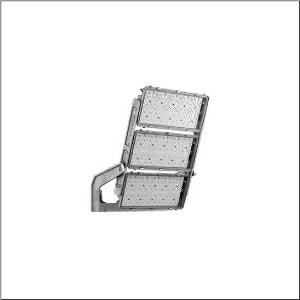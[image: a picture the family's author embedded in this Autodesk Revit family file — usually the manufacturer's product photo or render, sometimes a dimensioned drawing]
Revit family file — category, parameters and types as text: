
# Revit family: floodlight_fl_11_maxi_pro_remote___pl64_5xa779426v01aa_0b09
name_source: partatom
category: Lighting Fixtures
units: mm (PartAtom-declared; Revit-internal decimal feet)

## family parameters
Cut with Voids When Loaded = No
Host = Face
Light Source = No
Part Type = Normal
Room Calculation Point = No
Round Connector Dimension = Use Diameter
Shared = No

## types (1)
- --- (1 x LED, 216630 lm, 1539.7 W, 4000K)
    Apparent Load = 1540 VA
    CIE Flux Codes = 28 79 98 100 100
    Color Rendering = 70
    Color Temperature = 4000K
    Default Elevation = 1800 mm
    Description = Floodlight FL 11  maxi  pro Remote floodlight; light control with lens of PMMA; cover panel of toughened safety glass, transparent; light distribution: PL64, asymmetric direct distribution, LEDcolour temperature: 4000K, rated luminous flux: 216.630lm, colour rendering: CRI > 70, light colour: 740; luminous efficacy: 141lm/W; brightness control: DALI 2 (1 DALI address); with terminal, 8-pole, max. 2.5mm², mains connection: 220..240V/380..400V AC, 50/60Hz, surge voltage resistance: line to ground: 10kV, ECG replaceable separately, no afterglow with DALI off / DMX off command, LED unit replaceable without ESD environment, dustproof LED module, dimming range 10..100%; 1540W floodlight with 2x LED unit of diecast aluminium, coated grey; length: 713mm / width: 651mm / height: 338mm; mounting bracket, of diecast aluminium, uncoated, natural, equipment: Power, protection rating (complete): IP66; insulation class (complete): insulation class I (protective earthing); certification: CE, ENEC, VDE; ball protection: ball impact resistance with accessories, impact resistance: IK07; only for outdoor installations, rated ambient temperature 10°C, permissible operating ambient temperature: -40..+30°C, permissible storage temperature: -40..+85°Cpackaging unit: 1 piece

Light Distribution: PL64
    Height = 320 mm
    Lamp = 1 x LED
    Lamp Light Flux = 216630 lm
    Lamp Power = 1539.7 W
    Lamp count = 1
    Length = 1002 mm
    Luminous efficacy = 141 lm/W
    Manufacturer = Siteco
    ModVariant = No
    Model = 5XA779426V01AA
    Mounting Place = Ceiling
    Mounting Type = Surface mounted
    Number of Poles = 1
    OnlyDefault = Yes
    Power Factor = 1
    Product Name = Floodlight FL 11 maxi pro Remote | PL64
    Product group = floodlight | ceiling mounted
    ProductGroupID = 301
    Protection Class = Protection class I
    Protection Degree = IP 66
    RLX_Detail_Level = 1
    RLX_Emergency_Light_Flux = 0 lm
    RLX_Emergency_Type = 0
    RLX_Emergency_Type_DB = No
    RlxData = <blob elided: 52221 chars, md5=aefd5df7>
    Socket = socket
    Standby Power = 0 W
    System Light Flux = 216630 lm
    System Power = 1540 W
    Type Comments = factory setting: luminous flux: 100 % | dim-lin: 254 | 1080 mA
    Type Image = l_1349141.jpg
    URL = http://relux.com
    VarID = @adj_103068
    Voltage = 0 V
    Weight = 0.00 kg
    Width = 655 mm

## geometry (parser evidence)
native form markers: Blend x4, Sweep x14
no freeform markers — native parametric forms only
